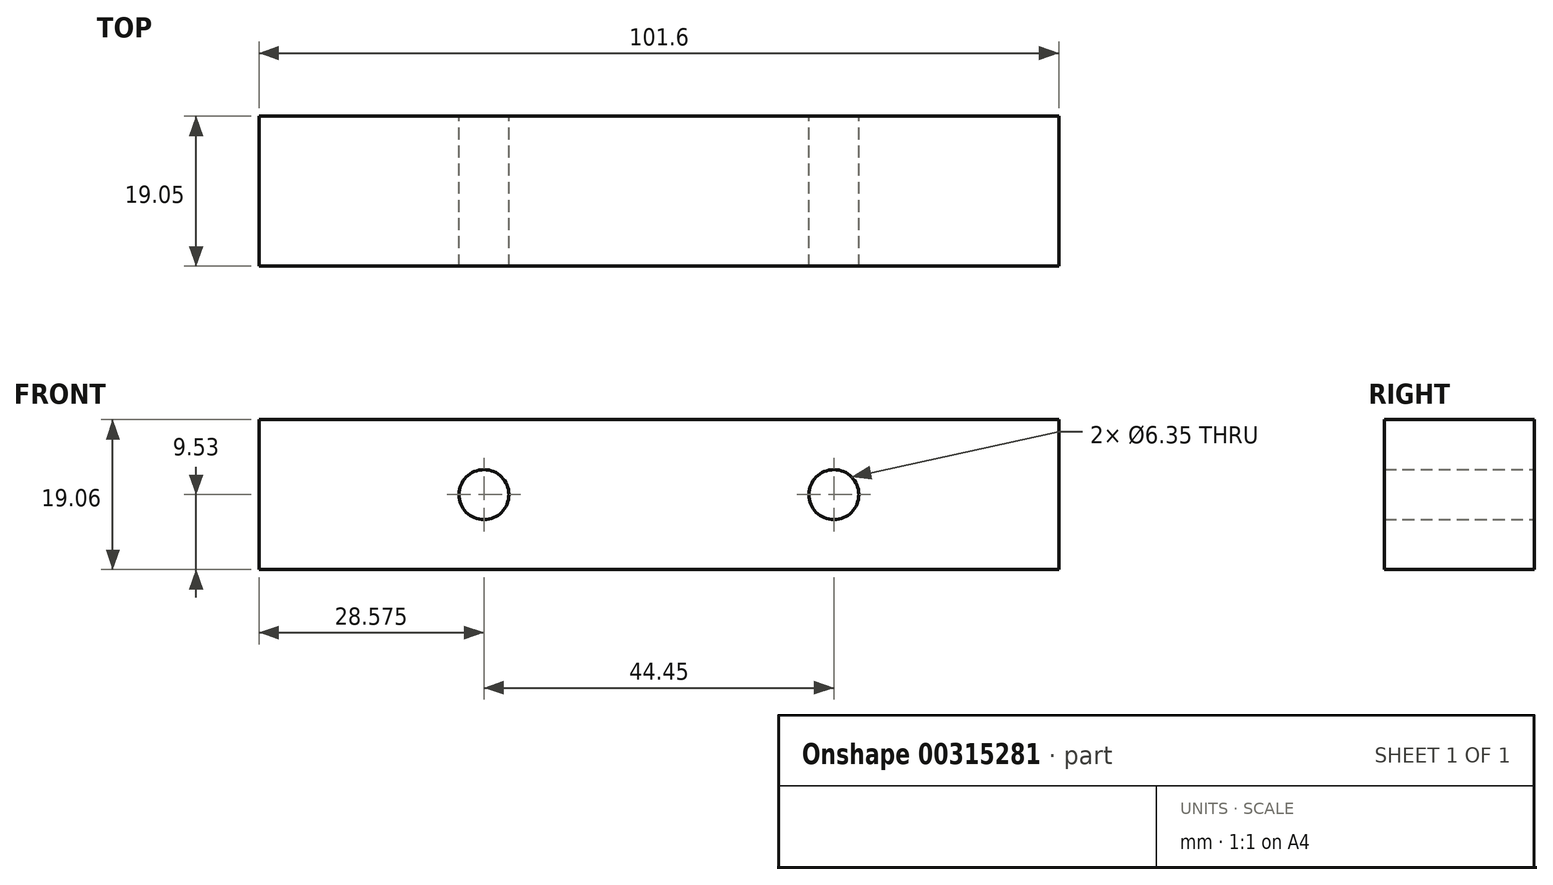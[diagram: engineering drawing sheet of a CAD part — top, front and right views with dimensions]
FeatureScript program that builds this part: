
annotation { "Feature Type Name" : "Feature", "Feature Type Description" : "" }
export const myFeature = defineFeature(function(context is Context, id is Id, definition is map)
    precondition{}
    {
        {
            var Q0;
            Q0=qCreatedBy(makeId("Front.planeOp"),FACE);
            var sketch = newSketch(context, id + "F0", { "sketchPlane" : qUnion([Q0])});
            skLineSegment(sketch, "E0", {"start": v(0, 0) * mm, "end": v(-2216.15, 0) * mm});
            skLineSegment(sketch, "E1", {"start": v(0, 0) * mm, "end": v(0, 2330.45) * mm});
            skLineSegment(sketch, "E2", {"start": v(-2216.15, -25.4) * mm, "end": v(12.7, -25.4) * mm, "construction": true});
            skLineSegment(sketch, "E3", {"start": v(0, 2330.45) * mm, "end": v(-2216.15, 2330.45) * mm});
            skLineSegment(sketch, "E4", {"start": v(-2216.15, 2330.45) * mm, "end": v(-2216.15, -25.4) * mm, "construction": true});
            skLineSegment(sketch, "E5", {"start": v(-2203.45, 2330.45) * mm, "end": v(-2203.45, -25.4) * mm});
            skLineSegment(sketch, "E6", {"start": v(12.7, 2205.48) * mm, "end": v(12.7, -25.4) * mm, "construction": true});
            skLineSegment(sketch, "E7.bottom", {"start": v(-1314.45, 876.3) * mm, "end": v(-19.05, 876.3) * mm});
            skLineSegment(sketch, "E7.top", {"start": v(-1314.45, 0) * mm, "end": v(-19.05, 0) * mm});
            skLineSegment(sketch, "E7.left", {"start": v(-1314.45, 876.3) * mm, "end": v(-1314.45, 0) * mm});
            skLineSegment(sketch, "E7.right", {"start": v(-19.05, 876.3) * mm, "end": v(-19.05, 0) * mm});
            skLineSegment(sketch, "E8.bottom", {"start": v(-19.05, 876.3) * mm, "end": v(0, 876.3) * mm});
            skLineSegment(sketch, "E8.top", {"start": v(-19.05, 114.3) * mm, "end": v(0, 114.3) * mm});
            skLineSegment(sketch, "E8.left", {"start": v(-19.05, 876.3) * mm, "end": v(-19.05, 114.3) * mm});
            skLineSegment(sketch, "E8.right", {"start": v(0, 876.3) * mm, "end": v(0, 114.3) * mm});
            skLineSegment(sketch, "E9.bottom", {"start": v(0, 876.3) * mm, "end": v(-1358.9, 876.3) * mm});
            skLineSegment(sketch, "E9.top", {"start": v(0, 996.95) * mm, "end": v(-1358.9, 996.95) * mm});
            skLineSegment(sketch, "E9.left", {"start": v(0, 876.3) * mm, "end": v(0, 996.95) * mm});
            skLineSegment(sketch, "E9.right", {"start": v(-1358.9, 876.3) * mm, "end": v(-1358.9, 996.95) * mm});
            skLineSegment(sketch, "E10", {"start": v(-1358.9, 908.05) * mm, "end": v(0, 908.05) * mm});
            skLineSegment(sketch, "E11.bottom", {"start": v(-1250.95, 1924.05) * mm, "end": v(-869.95, 1924.05) * mm});
            skLineSegment(sketch, "E11.top", {"start": v(-1250.95, 1162.05) * mm, "end": v(-869.95, 1162.05) * mm});
            skLineSegment(sketch, "E11.left", {"start": v(-1250.95, 1924.05) * mm, "end": v(-1250.95, 1162.05) * mm});
            skLineSegment(sketch, "E11.right", {"start": v(-869.95, 1924.05) * mm, "end": v(-869.95, 1162.05) * mm});
            skLineSegment(sketch, "E12.top", {"start": v(-869.95, 1165.1) * mm, "end": v(-488.95, 1165.1) * mm});
            skLineSegment(sketch, "E12.left", {"start": v(-869.95, 1924.05) * mm, "end": v(-869.95, 1165.1) * mm});
            skLineSegment(sketch, "E12.right", {"start": v(-488.95, 1924.05) * mm, "end": v(-488.95, 1165.1) * mm});
            skLineSegment(sketch, "E13.bottom", {"start": v(-488.95, 1924.05) * mm, "end": v(-107.95, 1924.05) * mm});
            skLineSegment(sketch, "E13.top", {"start": v(-488.95, 1162.05) * mm, "end": v(-107.95, 1162.05) * mm});
            skLineSegment(sketch, "E13.left", {"start": v(-488.95, 1924.05) * mm, "end": v(-488.95, 1162.05) * mm});
            skLineSegment(sketch, "E13.right", {"start": v(-107.95, 1924.05) * mm, "end": v(-107.95, 1162.05) * mm});
            skLineSegment(sketch, "E14", {"start": v(-679.45, 2330.45) * mm, "end": v(-679.45, 0) * mm, "construction": true});
            skPoint(sketch, "E15", {"position": v(-679.45, 996.95) * mm});
            skPoint(sketch, "E16", {"position": v(-679.45, 1165.1) * mm});
            skLineSegment(sketch, "E17.bottom", {"start": v(-1289.05, 2193.86) * mm, "end": v(-679.45, 2193.86) * mm});
            skLineSegment(sketch, "E17.top", {"start": v(-1289.05, 2063.69) * mm, "end": v(-679.45, 2063.69) * mm});
            skLineSegment(sketch, "E17.left", {"start": v(-1289.05, 2193.86) * mm, "end": v(-1289.05, 2063.69) * mm});
            skLineSegment(sketch, "E17.right", {"start": v(-679.45, 2193.86) * mm, "end": v(-679.45, 2063.69) * mm});
            skLineSegment(sketch, "E18.bottom", {"start": v(-679.45, 2193.86) * mm, "end": v(-69.85, 2193.86) * mm});
            skLineSegment(sketch, "E18.top", {"start": v(-679.45, 2063.69) * mm, "end": v(-69.85, 2063.69) * mm});
            skLineSegment(sketch, "E18.right", {"start": v(-69.85, 2193.86) * mm, "end": v(-69.85, 2063.69) * mm});
            skLineSegment(sketch, "E19", {"start": v(-679.45, 2063.69) * mm, "end": v(-679.45, 1927.1) * mm, "construction": true});
            skLineSegment(sketch, "E20", {"start": v(-679.45, 2330.45) * mm, "end": v(-679.45, 2193.86) * mm, "construction": true});
            skLineSegment(sketch, "E21", {"start": v(-127.25, 1169.67) * mm, "end": v(-127.25, 1022.54) * mm, "construction": true});
            skLineSegment(sketch, "E22", {"start": v(-1231.65, 1058.48) * mm, "end": v(-1231.65, 1020.22) * mm, "construction": true});
            skLineSegment(sketch, "E23", {"start": v(-469.9, 1169.67) * mm, "end": v(-469.9, 1021.38) * mm, "construction": true});
            skLineSegment(sketch, "E24", {"start": v(-889, 1058.48) * mm, "end": v(-889, 1021.38) * mm, "construction": true});
            skCircle(sketch, "E25", {"center": v(-344.02, 1462.79) * mm, "radius": 8.64 * mm});
            skLineSegment(sketch, "E26", {"start": v(-469.9, 1169.67) * mm, "end": v(-127.25, 1169.67) * mm});
            skLineSegment(sketch, "E27", {"start": v(-869.95, 1924.05) * mm, "end": v(-869.95, 1927.1) * mm});
            skLineSegment(sketch, "E28", {"start": v(-869.95, 1927.1) * mm, "end": v(-488.95, 1927.1) * mm});
            skLineSegment(sketch, "E29", {"start": v(-488.95, 1927.1) * mm, "end": v(-488.95, 1924.05) * mm});
            skLineSegment(sketch, "E30", {"start": v(-819.15, 1823.21) * mm, "end": v(-539.75, 1823.21) * mm});
            skPoint(sketch, "E31", {"position": v(-679.45, 1823.21) * mm});
            skLineSegment(sketch, "E32", {"start": v(-565.15, 1803.9) * mm, "end": v(-565.15, 1773.17) * mm});
            skLineSegment(sketch, "E33.MirrorCS", {"start": v(-793.75, 1803.9) * mm, "end": v(-793.75, 1773.17) * mm});
            skPoint(sketch, "E34", {"position": v(-793.75, 1788.54) * mm});
            skPoint(sketch, "E35", {"position": v(-565.15, 1788.54) * mm});
            skLineSegment(sketch, "E36", {"start": v(-252.3, 2125.89) * mm, "end": v(-252.3, 2131.23) * mm});
            skLineSegment(sketch, "E37", {"start": v(-247.65, 2131.23) * mm, "end": v(-247.65, 2125.89) * mm});
            skArc(sketch, "E38", {"start": v(-252.3, 2125.89) * mm, "mid": v(-249.97, 2119.06) * mm, "end": v(-247.65, 2125.89) * mm});
            skArc(sketch, "E39", {"start": v(-252.3, 2131.23) * mm, "mid": v(-249.97, 2133.56) * mm, "end": v(-247.65, 2131.23) * mm});
            skLineSegment(sketch, "E40", {"start": v(-249.97, 2131.23) * mm, "end": v(-249.97, 2122.87) * mm, "construction": true});
            skPoint(sketch, "E41", {"position": v(-374.65, 2193.86) * mm});
            skPoint(sketch, "E42", {"position": v(-374.65, 2063.69) * mm});
            skLineSegment(sketch, "E43", {"start": v(-374.65, 2193.86) * mm, "end": v(-374.65, 2063.69) * mm, "construction": true});
            skLineSegment(sketch, "E44.MirrorCS", {"start": v(-497, 2125.89) * mm, "end": v(-497, 2131.23) * mm});
            skLineSegment(sketch, "E45.MirrorCS", {"start": v(-501.65, 2131.23) * mm, "end": v(-501.65, 2125.89) * mm});
            skArc(sketch, "E46.MirrorCS", {"start": v(-497, 2125.89) * mm, "mid": v(-499.33, 2119.06) * mm, "end": v(-501.65, 2125.89) * mm});
            skArc(sketch, "E47.MirrorCS", {"start": v(-497, 2131.23) * mm, "mid": v(-499.33, 2133.56) * mm, "end": v(-501.65, 2131.23) * mm});
            skLineSegment(sketch, "E48.MirrorCS", {"start": v(-857.25, 2131.23) * mm, "end": v(-857.25, 2125.89) * mm});
            skArc(sketch, "E49.MirrorCS", {"start": v(-861.9, 2125.89) * mm, "mid": v(-859.57, 2119.06) * mm, "end": v(-857.25, 2125.89) * mm});
            skLineSegment(sketch, "E50.MirrorCS", {"start": v(-861.9, 2125.89) * mm, "end": v(-861.9, 2131.23) * mm});
            skArc(sketch, "E51.MirrorCS", {"start": v(-861.9, 2131.23) * mm, "mid": v(-859.57, 2133.56) * mm, "end": v(-857.25, 2131.23) * mm});
            skArc(sketch, "E52.MirrorCS", {"start": v(-1106.6, 2125.89) * mm, "mid": v(-1108.93, 2119.06) * mm, "end": v(-1111.25, 2125.89) * mm});
            skLineSegment(sketch, "E53.MirrorCS", {"start": v(-1111.25, 2131.23) * mm, "end": v(-1111.25, 2125.89) * mm});
            skLineSegment(sketch, "E54.MirrorCS", {"start": v(-1106.6, 2125.89) * mm, "end": v(-1106.6, 2131.23) * mm});
            skArc(sketch, "E55.MirrorCS", {"start": v(-1106.6, 2131.23) * mm, "mid": v(-1108.93, 2133.56) * mm, "end": v(-1111.25, 2131.23) * mm});
            skPoint(sketch, "E56", {"position": v(-374.65, 2128.77) * mm});
            skCircle(sketch, "E57", {"center": v(-374.65, 2128.77) * mm, "radius": 12.7 * mm});
            skCircle(sketch, "E58.MirrorC", {"center": v(-984.25, 2128.77) * mm, "radius": 12.7 * mm});
            skCircle(sketch, "E59", {"center": v(-649.29, 449.26) * mm, "radius": 7.94 * mm});
            skCircle(sketch, "E60", {"center": v(-931.86, 439.74) * mm, "radius": 7.94 * mm});
            skCircle(sketch, "E61", {"center": v(-1947.86, 80.96) * mm, "radius": 7.94 * mm});
            skCircle(sketch, "E62", {"center": v(-749.05, 454.28) * mm, "radius": 28.32 * mm});
            skLineSegment(sketch, "E63", {"start": v(-657.23, 0) * mm, "end": v(-657.23, 34.73) * mm});
            skLineSegment(sketch, "E64", {"start": v(-641.35, 34.73) * mm, "end": v(-641.35, 0) * mm});
            skArc(sketch, "E65", {"start": v(-657.23, 34.73) * mm, "mid": v(-649.29, 42.67) * mm, "end": v(-641.35, 34.73) * mm});
            skLineSegment(sketch, "E66", {"start": v(-786.9, 0) * mm, "end": v(-786.9, 70.1) * mm});
            skArc(sketch, "E67", {"start": v(-786.9, 70.1) * mm, "mid": v(-758.57, 98.42) * mm, "end": v(-730.25, 70.1) * mm});
            skLineSegment(sketch, "E68", {"start": v(-730.25, 70.1) * mm, "end": v(-730.25, 0) * mm});
            skLineSegment(sketch, "E69", {"start": v(-939.8, 0) * mm, "end": v(-939.8, 34.73) * mm});
            skLineSegment(sketch, "E70", {"start": v(-923.92, 0) * mm, "end": v(-923.92, 34.73) * mm});
            skArc(sketch, "E71", {"start": v(-939.8, 34.73) * mm, "mid": v(-931.86, 42.67) * mm, "end": v(-923.92, 34.73) * mm});
            skPoint(sketch, "E72", {"position": v(-679.45, 2128.77) * mm});
            skCircle(sketch, "E73", {"center": v(-679.45, 2128.77) * mm, "radius": 50.8 * mm});
            skLineSegment(sketch, "E74", {"start": v(-701.6, 2083.05) * mm, "end": v(-657.3, 2083.05) * mm});
            skSolve(sketch);
        }
        {
            var Q0;
            Q0=qCreatedBy(makeId("Front.planeOp"),FACE);
            var sketch = newSketch(context, id + "F1", { "sketchPlane" : qUnion([Q0])});
            skPoint(sketch, "E75.0", {"position": v(0, 2330.45) * mm});
            skLineSegment(sketch, "E76", {"start": v(0, 2330.45) * mm, "end": v(0, -15.87) * mm});
            skLineSegment(sketch, "E77", {"start": v(0, -15.87) * mm, "end": v(-2228.83, -6.35) * mm});
            skLineSegment(sketch, "E78", {"start": v(0, -15.87) * mm, "end": v(-2228.83, -15.87) * mm, "construction": true});
            skLineSegment(sketch, "E79", {"start": v(0, 2330.45) * mm, "end": v(-2224.03, 2349.5) * mm});
            skLineSegment(sketch, "E80", {"start": v(-2228.83, -6.35) * mm, "end": v(-2224.03, 2349.5) * mm});
            skLineSegment(sketch, "E81", {"start": v(-2228.83, -6.35) * mm, "end": v(-2228.83, 2349.5) * mm, "construction": true});
            skLineSegment(sketch, "E82", {"start": v(-2228.83, 2349.5) * mm, "end": v(0, 2349.5) * mm, "construction": true});
            skLineSegment(sketch, "E83", {"start": v(-2224.14, 2292.35) * mm, "end": v(0, 2271.71) * mm});
            skLineSegment(sketch, "E84", {"start": v(-2228.75, 31.75) * mm, "end": v(0, 22.23) * mm});
            skLineSegment(sketch, "E85", {"start": v(-38.1, 2272.07) * mm, "end": v(-38.1, 22.39) * mm});
            skLineSegment(sketch, "E86", {"start": v(-209.55, 2273.66) * mm, "end": v(-184.15, 23.01) * mm});
            skLineSegment(sketch, "E87", {"start": v(-247.66, 2274.01) * mm, "end": v(-222.25, 23.18) * mm});
            skLineSegment(sketch, "E88", {"start": v(-584.2, 2277.13) * mm, "end": v(-568.33, 24.65) * mm});
            skLineSegment(sketch, "E89", {"start": v(-622.3, 2277.49) * mm, "end": v(-606.43, 24.82) * mm});
            skLineSegment(sketch, "E90", {"start": v(-987.43, 2280.87) * mm, "end": v(-993.78, 26.47) * mm});
            skLineSegment(sketch, "E91", {"start": v(-1025.52, 2281.23) * mm, "end": v(-1031.87, 26.64) * mm});
            skLineSegment(sketch, "E92", {"start": v(-1393.83, 2284.64) * mm, "end": v(-1403.35, 28.22) * mm});
            skLineSegment(sketch, "E93", {"start": v(-1431.92, 2285) * mm, "end": v(-1441.45, 28.39) * mm});
            skLineSegment(sketch, "E94", {"start": v(-1803.4, 2288.45) * mm, "end": v(-1806.58, 29.95) * mm});
            skLineSegment(sketch, "E95", {"start": v(-1841.5, 2288.8) * mm, "end": v(-1844.67, 30.1) * mm});
            skLineSegment(sketch, "E96", {"start": v(-2201.92, 2292.14) * mm, "end": v(-2206.53, 31.66) * mm});
            skLineSegment(sketch, "E97", {"start": v(-1844.62, 68.2) * mm, "end": v(-1806.52, 68.05) * mm});
            skLineSegment(sketch, "E98", {"start": v(-1441.29, 66.49) * mm, "end": v(-1403.19, 66.32) * mm});
            skLineSegment(sketch, "E99", {"start": v(-1031.8, 52.04) * mm, "end": v(-993.7, 51.87) * mm});
            skLineSegment(sketch, "E100", {"start": v(-606.6, 50.22) * mm, "end": v(-568.5, 50.06) * mm});
            skLineSegment(sketch, "E101", {"start": v(-222.68, 61.28) * mm, "end": v(-184.58, 61.11) * mm});
            skLineSegment(sketch, "E102", {"start": v(-38.1, 60.49) * mm, "end": v(0, 60.33) * mm});
            skLineSegment(sketch, "E103", {"start": v(-957.73, 305.77) * mm, "end": v(-957.28, 467.7) * mm});
            skLineSegment(sketch, "E104", {"start": v(-957.28, 467.7) * mm, "end": v(-992.53, 467.8) * mm});
            skLineSegment(sketch, "E105", {"start": v(-992.99, 305.87) * mm, "end": v(-957.73, 305.77) * mm});
            skLineSegment(sketch, "E106", {"start": v(-608.55, 326.45) * mm, "end": v(-643.83, 291.68) * mm});
            skLineSegment(sketch, "E107", {"start": v(-643.83, 291.68) * mm, "end": v(-645.4, 512.74) * mm});
            skLineSegment(sketch, "E108", {"start": v(-645.4, 512.74) * mm, "end": v(-609.87, 513) * mm});
            skSolve(sketch);
        }
        {
            var Q0;
            Q0=qCreatedBy(makeId("Front.planeOp"),FACE);
            var sketch = newSketch(context, id + "F2", { "sketchPlane" : qUnion([Q0])});
            skPoint(sketch, "E109.0", {"position": v(-2216.15, 2330.45) * mm});
            skPoint(sketch, "E110.0", {"position": v(12.7, 2205.48) * mm});
            skPoint(sketch, "E111.0", {"position": v(-344.02, 1462.79) * mm});
            skCircle(sketch, "E112.0", {"center": v(-344.02, 1462.79) * mm, "radius": 8.64 * mm, "construction": true});
            skLineSegment(sketch, "E113.bottom", {"start": v(-2216.15, 2330.45) * mm, "end": v(12.7, 2330.45) * mm});
            skLineSegment(sketch, "E113.top", {"start": v(-2216.15, 1111.25) * mm, "end": v(12.7, 1111.25) * mm});
            skLineSegment(sketch, "E113.left", {"start": v(-2216.15, 2330.45) * mm, "end": v(-2216.15, 1111.25) * mm});
            skLineSegment(sketch, "E113.right", {"start": v(12.7, 2330.45) * mm, "end": v(12.7, 1111.25) * mm});
            skLineSegment(sketch, "E114.top", {"start": v(-2216.15, -25.4) * mm, "end": v(12.7, -25.4) * mm});
            skLineSegment(sketch, "E114.left", {"start": v(-2216.15, 1111.25) * mm, "end": v(-2216.15, -25.4) * mm});
            skLineSegment(sketch, "E114.right", {"start": v(12.7, 1111.25) * mm, "end": v(12.7, -25.4) * mm});
            skPoint(sketch, "E115.0", {"position": v(-2216.15, -25.4) * mm});
            skPoint(sketch, "E116.0", {"position": v(12.7, -25.4) * mm});
            skLineSegment(sketch, "E117.0", {"start": v(-939.8, 0) * mm, "end": v(-939.8, 34.73) * mm, "construction": true});
            skLineSegment(sketch, "E118.0", {"start": v(-923.92, 0) * mm, "end": v(-923.92, 34.73) * mm, "construction": true});
            skArc(sketch, "E119.0", {"start": v(-939.8, 34.73) * mm, "mid": v(-931.86, 42.67) * mm, "end": v(-923.92, 34.73) * mm, "construction": true});
            skLineSegment(sketch, "E120.0", {"start": v(-786.9, 0) * mm, "end": v(-786.9, 70.1) * mm, "construction": true});
            skLineSegment(sketch, "E121.0", {"start": v(-730.25, 70.1) * mm, "end": v(-730.25, 0) * mm, "construction": true});
            skArc(sketch, "E122.0", {"start": v(-786.9, 70.1) * mm, "mid": v(-758.57, 98.42) * mm, "end": v(-730.25, 70.1) * mm, "construction": true});
            skLineSegment(sketch, "E123.0", {"start": v(-657.23, 0) * mm, "end": v(-657.23, 34.73) * mm, "construction": true});
            skLineSegment(sketch, "E124.0", {"start": v(-641.35, 34.73) * mm, "end": v(-641.35, 0) * mm, "construction": true});
            skArc(sketch, "E125.0", {"start": v(-657.23, 34.73) * mm, "mid": v(-649.29, 42.67) * mm, "end": v(-641.35, 34.73) * mm, "construction": true});
            skLineSegment(sketch, "E126", {"start": v(-944.56, -25.4) * mm, "end": v(-944.56, 34.73) * mm});
            skLineSegment(sketch, "E127", {"start": v(-919.16, -25.4) * mm, "end": v(-919.16, 34.73) * mm});
            skArc(sketch, "E128", {"start": v(-944.56, 34.73) * mm, "mid": v(-931.86, 47.43) * mm, "end": v(-919.16, 34.73) * mm});
            skLineSegment(sketch, "E129", {"start": v(-796.67, -25.4) * mm, "end": v(-796.67, 70.1) * mm});
            skLineSegment(sketch, "E130", {"start": v(-720.47, -25.4) * mm, "end": v(-720.47, 70.1) * mm});
            skLineSegment(sketch, "E131", {"start": v(-661.99, -25.4) * mm, "end": v(-661.99, 34.73) * mm});
            skLineSegment(sketch, "E132", {"start": v(-636.59, -25.4) * mm, "end": v(-636.59, 34.73) * mm});
            skArc(sketch, "E133", {"start": v(-796.67, 70.1) * mm, "mid": v(-758.57, 108.2) * mm, "end": v(-720.47, 70.1) * mm});
            skArc(sketch, "E134", {"start": v(-661.99, 34.73) * mm, "mid": v(-649.29, 47.43) * mm, "end": v(-636.59, 34.73) * mm});
            skCircle(sketch, "E135.0", {"center": v(-931.86, 439.74) * mm, "radius": 7.94 * mm, "construction": true});
            skCircle(sketch, "E136.0", {"center": v(-749.05, 454.28) * mm, "radius": 28.32 * mm, "construction": true});
            skCircle(sketch, "E137.0", {"center": v(-649.29, 449.26) * mm, "radius": 7.94 * mm, "construction": true});
            skCircle(sketch, "E138.0", {"center": v(-1947.86, 80.96) * mm, "radius": 7.94 * mm, "construction": true});
            skCircle(sketch, "E139", {"center": v(-931.86, 439.74) * mm, "radius": 12.7 * mm});
            skCircle(sketch, "E140", {"center": v(-749.05, 454.28) * mm, "radius": 38.1 * mm});
            skCircle(sketch, "E141", {"center": v(-649.29, 449.26) * mm, "radius": 12.7 * mm});
            skCircle(sketch, "E142", {"center": v(-1947.86, 80.96) * mm, "radius": 12.7 * mm});
            skCircle(sketch, "E143", {"center": v(-344.02, 1462.79) * mm, "radius": 12.7 * mm});
            skSolve(sketch);
        }
        {
            var Q0;
            Q0=qCreatedBy(makeId("Front.planeOp"),FACE);
            var sketch = newSketch(context, id + "F3", { "sketchPlane" : qUnion([Q0])});
            skLineSegment(sketch, "E144.bottom", {"start": v(31.75, -9.52) * mm, "end": v(-31.75, -9.53) * mm});
            skLineSegment(sketch, "E144.top", {"start": v(31.75, 9.53) * mm, "end": v(-31.75, 9.53) * mm});
            skLineSegment(sketch, "E144.left", {"start": v(31.75, -9.52) * mm, "end": v(31.75, 9.53) * mm});
            skLineSegment(sketch, "E144.right", {"start": v(-31.75, -9.53) * mm, "end": v(-31.75, 9.53) * mm});
            skPoint(sketch, "E144.middle", {"position": v(0, 0) * mm});
            skCircle(sketch, "E145", {"center": v(-22.22, 0) * mm, "radius": 3.18 * mm});
            skLineSegment(sketch, "E146", {"start": v(0, 9.53) * mm, "end": v(0, -9.52) * mm, "construction": true});
            skLineSegment(sketch, "E147", {"start": v(-22.22, 0) * mm, "end": v(-22.23, 9.53) * mm, "construction": true});
            skLineSegment(sketch, "E148", {"start": v(-22.23, 9.53) * mm, "end": v(-22.22, 0) * mm, "construction": true});
            skLineSegment(sketch, "E149", {"start": v(-22.22, -9.52) * mm, "end": v(-22.22, 0) * mm, "construction": true});
            skLineSegment(sketch, "E150", {"start": v(-22.22, 0) * mm, "end": v(-31.75, 0) * mm, "construction": true});
            skCircle(sketch, "E151.MirrorC", {"center": v(22.22, 0) * mm, "radius": 3.18 * mm});
            skLineSegment(sketch, "E152", {"start": v(-31.75, 9.53) * mm, "end": v(-50.8, 9.53) * mm});
            skLineSegment(sketch, "E153", {"start": v(-50.8, 9.53) * mm, "end": v(-50.8, -9.53) * mm});
            skLineSegment(sketch, "E154", {"start": v(-31.75, 0) * mm, "end": v(-41.27, 0) * mm, "construction": true});
            skLineSegment(sketch, "E155", {"start": v(-41.27, 0) * mm, "end": v(-50.8, 0) * mm, "construction": true});
            skLineSegment(sketch, "E156", {"start": v(-50.8, -9.53) * mm, "end": v(-31.75, -9.53) * mm});
            skLineSegment(sketch, "E157.bottom", {"start": v(-38.1, -9.53) * mm, "end": v(-44.45, -9.53) * mm, "construction": true});
            skLineSegment(sketch, "E157.top", {"start": v(-38.1, 9.53) * mm, "end": v(-44.45, 9.53) * mm, "construction": true});
            skLineSegment(sketch, "E157.left", {"start": v(-38.1, -9.53) * mm, "end": v(-38.1, 9.53) * mm, "construction": true});
            skLineSegment(sketch, "E157.right", {"start": v(-44.45, -9.52) * mm, "end": v(-44.45, 9.53) * mm, "construction": true});
            skPoint(sketch, "E157.middle", {"position": v(-41.27, 0) * mm});
            skLineSegment(sketch, "E158.MirrorCS", {"start": v(31.75, 9.53) * mm, "end": v(50.8, 9.53) * mm});
            skLineSegment(sketch, "E159.MirrorCS", {"start": v(50.8, 9.53) * mm, "end": v(50.8, -9.53) * mm});
            skLineSegment(sketch, "E160.MirrorCS", {"start": v(50.8, -9.53) * mm, "end": v(31.75, -9.52) * mm});
            skLineSegment(sketch, "E161.MirrorCS", {"start": v(38.1, -9.52) * mm, "end": v(38.1, 9.53) * mm, "construction": true});
            skLineSegment(sketch, "E162.MirrorCS", {"start": v(44.45, -9.52) * mm, "end": v(44.45, 9.53) * mm, "construction": true});
            skSolve(sketch);
        }
        {
            var Q0;
            Q0 = qSketchRegion(id + "F3", true);
            extrude(context, id + "F4", {"entities" : qUnion([Q0]), "depth" : 19.05 * mm});
        }
    });
